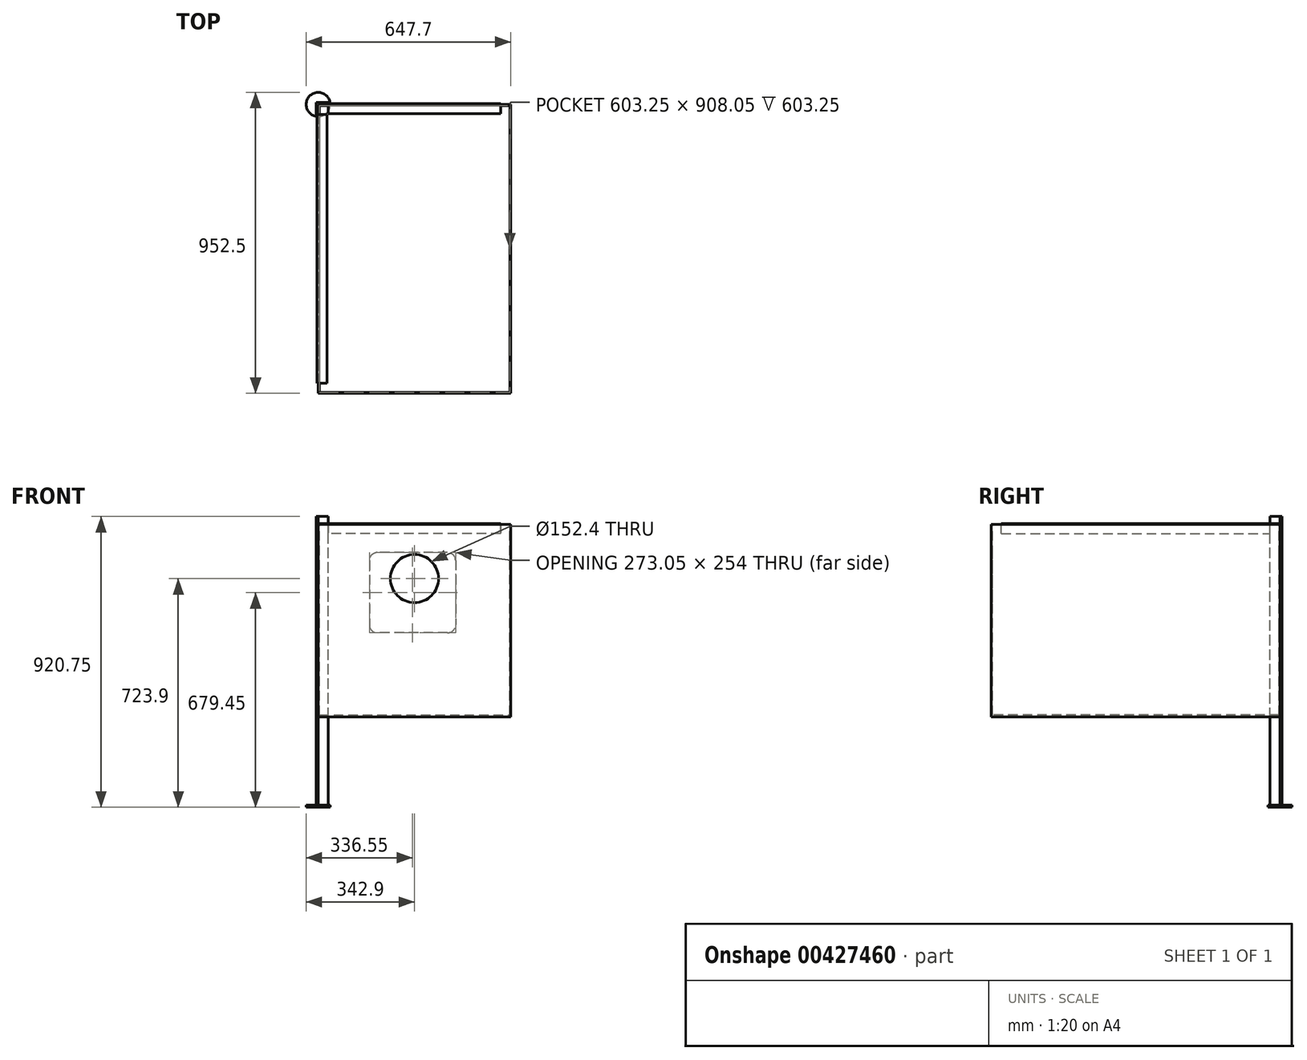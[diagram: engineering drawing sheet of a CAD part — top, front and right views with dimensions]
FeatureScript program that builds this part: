
annotation { "Feature Type Name" : "Feature", "Feature Type Description" : "" }
export const myFeature = defineFeature(function(context is Context, id is Id, definition is map)
    precondition{}
    {
        {
            var Q0;
            Q0=qCreatedBy(makeId("Top.planeOp"),FACE);
            var sketch = newSketch(context, id + "F0", { "sketchPlane" : qUnion([Q0])});
            skLineSegment(sketch, "E0.bottom", {"start": v(0, 0) * mm, "end": v(609.6, 0) * mm});
            skLineSegment(sketch, "E0.top", {"start": v(0, -914.4) * mm, "end": v(609.6, -914.4) * mm});
            skLineSegment(sketch, "E0.left", {"start": v(0, 0) * mm, "end": v(0, -914.4) * mm});
            skLineSegment(sketch, "E0.right", {"start": v(609.6, 0) * mm, "end": v(609.6, -914.4) * mm});
            skSolve(sketch);
        }
        {
            var Q0;
            Q0 = qSketchRegion(id + "F0", true);
            extrude(context, id + "F1", {"entities" : qUnion([Q0]), "depth" : 609.6 * mm});
        }
        {
            var Q0;
            Q0=makeQuery(id+"F1.opExtrude","CAP_FACE",FACE,{"disambiguationData":[OSD([sQuery(id+"F0.wireOp",EDGE,"E0.bottom"),sQuery(id+"F0.wireOp",EDGE,"E0.top"),sQuery(id+"F0.wireOp",EDGE,"E0.left"),sQuery(id+"F0.wireOp",EDGE,"E0.right")])],"isStart":false});
            var sketch = newSketch(context, id + "F2", { "sketchPlane" : qUnion([Q0])});
            skLineSegment(sketch, "E1.bottom", {"start": v(3.17, -3.17) * mm, "end": v(606.43, -3.17) * mm});
            skLineSegment(sketch, "E1.top", {"start": v(3.17, -911.23) * mm, "end": v(606.43, -911.23) * mm});
            skLineSegment(sketch, "E1.left", {"start": v(3.18, -3.18) * mm, "end": v(3.18, -911.23) * mm});
            skLineSegment(sketch, "E1.right", {"start": v(606.43, -3.17) * mm, "end": v(606.43, -911.22) * mm});
            skSolve(sketch);
        }
        {
            var Q0;
            Q0=makeQuery(id+"F2.imprint","IMPRINT",FACE,{"disambiguationData":[TD([[makeQuery(id+"F2.imprint","IMPRINT",EDGE,{"derivedFrom":sQuery(id+"F2.wireOp",EDGE,"E1.bottom")}),-1.0]])]});
            extrude(context, id + "F3", {"entities" : qUnion([Q0]), "operationType" : NewBodyOperationType.REMOVE, "oppositeDirection" : true, "depth" : 603.25 * mm});
        }
        {
            var Q0;
            Q0=makeQuery(id+"F1.opExtrude","SWEPT_FACE",FACE,{"disambiguationData":[OSD([sQuery(id+"F0.wireOp",EDGE,"E0.top")])]});
            var sketch = newSketch(context, id + "F4", { "sketchPlane" : qUnion([Q0])});
            skCircle(sketch, "E2", {"center": v(304.8, 438.15) * mm, "radius": 76.2 * mm});
            skSolve(sketch);
        }
        {
            var Q0;
            Q0=makeQuery(id+"F4.imprint","IMPRINT",FACE,{"disambiguationData":[TD([[makeQuery(id+"F4.imprint","IMPRINT",EDGE,{"derivedFrom":sQuery(id+"F4.wireOp",EDGE,"E2")}),1.0]])]});
            extrude(context, id + "F5", {"entities" : qUnion([Q0]), "operationType" : NewBodyOperationType.REMOVE, "oppositeDirection" : true, "depth" : 3.17 * mm});
        }
        {
            var Q0;
            Q0=makeQuery(id+"F1.opExtrude","CAP_FACE",FACE,{"disambiguationData":[OSD([sQuery(id+"F0.wireOp",EDGE,"E0.bottom"),sQuery(id+"F0.wireOp",EDGE,"E0.top"),sQuery(id+"F0.wireOp",EDGE,"E0.left"),sQuery(id+"F0.wireOp",EDGE,"E0.right")])],"isStart":false});
            var sketch = newSketch(context, id + "F6", { "sketchPlane" : qUnion([Q0])});
            skLineSegment(sketch, "E3", {"start": v(0, -31.75) * mm, "end": v(-6.35, -31.75) * mm});
            skLineSegment(sketch, "E4", {"start": v(-6.35, -31.75) * mm, "end": v(-6.35, 6.35) * mm});
            skLineSegment(sketch, "E5", {"start": v(-6.35, 6.35) * mm, "end": v(31.75, 6.35) * mm});
            skLineSegment(sketch, "E6", {"start": v(31.75, 6.35) * mm, "end": v(31.75, 0) * mm});
            skSolve(sketch);
        }
        {
            var Q0;
            {var subQ4=sQuery(id+"F6.wireOp",EDGE,"E3");Q0=makeQuery(id+"F6.imprint","IMPRINT",FACE,{"disambiguationData":[TD([[makeQuery(id+"F6.imprint","IMPRINT",EDGE,{"derivedFrom":subQ4}),-1.0]])]});}
            extrude(context, id + "F7", {"entities" : qUnion([Q0]), "oppositeDirection" : true, "depth" : 889 * mm});
        }
        {
            var Q0;
            Q0=makeQuery(id+"F7.opExtrude","CAP_FACE",FACE,{"disambiguationData":[OSD([sQuery(id+"F0.wireOp",EDGE,"E0.bottom"),sQuery(id+"F0.wireOp",EDGE,"E0.left"),sQuery(id+"F6.wireOp",EDGE,"E3"),sQuery(id+"F6.wireOp",EDGE,"E4"),sQuery(id+"F6.wireOp",EDGE,"E5"),sQuery(id+"F6.wireOp",EDGE,"E6")])],"isStart":true});
            extrude(context, id + "F8", {"entities" : qUnion([Q0]), "operationType" : NewBodyOperationType.ADD, "depth" : 25.4 * mm});
        }
        {
            var Q0;
            Q0=makeQuery(id+"F7.opExtrude","CAP_FACE",FACE,{"disambiguationData":[OSD([sQuery(id+"F0.wireOp",EDGE,"E0.bottom"),sQuery(id+"F0.wireOp",EDGE,"E0.left"),sQuery(id+"F6.wireOp",EDGE,"E3"),sQuery(id+"F6.wireOp",EDGE,"E4"),sQuery(id+"F6.wireOp",EDGE,"E5"),sQuery(id+"F6.wireOp",EDGE,"E6")])],"isStart":false});
            var sketch = newSketch(context, id + "F9", { "sketchPlane" : qUnion([Q0])});
            skCircle(sketch, "E7", {"center": v(0, 0) * mm, "radius": 38.1 * mm});
            skSolve(sketch);
        }
        {
            var Q0;
            Q0 = qSketchRegion(id + "F9", true);
            extrude(context, id + "F10", {"entities" : qUnion([Q0]), "operationType" : NewBodyOperationType.ADD, "depth" : 6.35 * mm});
        }
        {
            var Q0;
            Q0=makeQuery(id+"F1.opExtrude","SWEPT_FACE",FACE,{"disambiguationData":[OSD([sQuery(id+"F0.wireOp",EDGE,"E0.bottom")])]});
            var sketch = newSketch(context, id + "F11", { "sketchPlane" : qUnion([Q0])});
            skLineSegment(sketch, "E8.bottom", {"start": v(-409.58, 520.7) * mm, "end": v(-187.32, 520.7) * mm});
            skLineSegment(sketch, "E8.top", {"start": v(-409.58, 266.7) * mm, "end": v(-187.32, 266.7) * mm});
            skLineSegment(sketch, "E8.left", {"start": v(-434.98, 495.3) * mm, "end": v(-434.98, 292.1) * mm});
            skLineSegment(sketch, "E8.right", {"start": v(-161.92, 495.3) * mm, "end": v(-161.92, 292.1) * mm});
            skPoint(sketch, "E9.visualSharp", {"position": v(-434.98, 520.7) * mm});
            skArc(sketch, "E9.filletArc", {"start": v(-409.58, 520.7) * mm, "mid": v(-427.54, 513.26) * mm, "end": v(-434.98, 495.3) * mm});
            skPoint(sketch, "E10.visualSharp", {"position": v(-161.92, 520.7) * mm});
            skArc(sketch, "E10.filletArc", {"start": v(-161.92, 495.3) * mm, "mid": v(-169.36, 513.26) * mm, "end": v(-187.32, 520.7) * mm});
            skPoint(sketch, "E11.visualSharp", {"position": v(-161.92, 266.7) * mm});
            skArc(sketch, "E11.filletArc", {"start": v(-187.32, 266.7) * mm, "mid": v(-169.36, 274.14) * mm, "end": v(-161.92, 292.1) * mm});
            skPoint(sketch, "E12.visualSharp", {"position": v(-434.98, 266.7) * mm});
            skArc(sketch, "E12.filletArc", {"start": v(-434.98, 292.1) * mm, "mid": v(-427.54, 274.14) * mm, "end": v(-409.58, 266.7) * mm});
            skSolve(sketch);
        }
        {
            var Q0;
            Q0=makeQuery(id+"F11.imprint","IMPRINT",FACE,{"disambiguationData":[TD([[makeQuery(id+"F11.imprint","IMPRINT",EDGE,{"derivedFrom":sQuery(id+"F11.wireOp",EDGE,"E8.bottom")}),-1.0]])]});
            extrude(context, id + "F12", {"entities" : qUnion([Q0]), "operationType" : NewBodyOperationType.REMOVE, "oppositeDirection" : true, "depth" : 3.17 * mm});
        }
        {
            var Q0;
            {var subQ0=sQuery(id+"F6.wireOp",EDGE,"E6");Q0=makeQuery(id+"F8.boolean.opBoolean","MERGE",FACE,{"derivedFrom":[makeQuery(id+"F7.opExtrude","SWEPT_FACE",FACE,{"disambiguationData":[OSD([subQ0])]}),makeQuery(id+"F8.opExtrude","SWEPT_FACE",FACE,{"disambiguationData":[OSD([subQ0])]})]});}
            var sketch = newSketch(context, id + "F13", { "sketchPlane" : qUnion([Q0])});
            skLineSegment(sketch, "E13", {"start": v(0, 581.02) * mm, "end": v(0, 609.6) * mm});
            skLineSegment(sketch, "E14", {"start": v(0, 609.6) * mm, "end": v(-28.58, 609.6) * mm});
            skLineSegment(sketch, "E15", {"start": v(-28.58, 609.6) * mm, "end": v(-28.58, 612.77) * mm});
            skLineSegment(sketch, "E16", {"start": v(-28.58, 612.77) * mm, "end": v(3.17, 612.77) * mm});
            skLineSegment(sketch, "E17", {"start": v(3.17, 612.77) * mm, "end": v(3.17, 581.02) * mm});
            skLineSegment(sketch, "E18", {"start": v(3.17, 581.02) * mm, "end": v(0, 581.02) * mm});
            skSolve(sketch);
        }
        {
            var Q0;
            {var subQ6=sQuery(id+"F13.wireOp",EDGE,"E13");Q0=makeQuery(id+"F13.imprint","IMPRINT",FACE,{"disambiguationData":[TD([[makeQuery(id+"F13.imprint","IMPRINT",EDGE,{"derivedFrom":subQ6}),-1.0]])]});}
            var Q1;
            {var subQ0=sQuery(id+"F13.wireOp",EDGE,"E14");Q1=makeQuery(id+"F13.imprint","IMPRINT",FACE,{"disambiguationData":[TD([[makeQuery(id+"F13.imprint","IMPRINT",EDGE,{"derivedFrom":subQ0}),-1.0]])]});}
            extrude(context, id + "F14", {"entities" : qUnion([Q0, Q1]), "depth" : 546.1 * mm});
        }
        {
            var Q0;
            {var subQ0=sQuery(id+"F6.wireOp",EDGE,"E3");Q0=makeQuery(id+"F8.boolean.opBoolean","MERGE",FACE,{"derivedFrom":[makeQuery(id+"F7.opExtrude","SWEPT_FACE",FACE,{"disambiguationData":[OSD([subQ0])]}),makeQuery(id+"F8.opExtrude","SWEPT_FACE",FACE,{"disambiguationData":[OSD([subQ0])]})]});}
            var sketch = newSketch(context, id + "F15", { "sketchPlane" : qUnion([Q0])});
            skLineSegment(sketch, "E19", {"start": v(28.57, 609.6) * mm, "end": v(0, 609.6) * mm});
            skLineSegment(sketch, "E20", {"start": v(0, 609.6) * mm, "end": v(0, 581.02) * mm});
            skLineSegment(sketch, "E21", {"start": v(0, 581.02) * mm, "end": v(-3.18, 581.02) * mm});
            skLineSegment(sketch, "E22", {"start": v(-3.18, 581.02) * mm, "end": v(-3.18, 612.77) * mm});
            skLineSegment(sketch, "E23", {"start": v(-3.18, 612.77) * mm, "end": v(28.57, 612.77) * mm});
            skLineSegment(sketch, "E24", {"start": v(28.58, 612.77) * mm, "end": v(28.58, 609.6) * mm});
            skSolve(sketch);
        }
        {
            var Q0;
            {var subQ6=sQuery(id+"F15.wireOp",EDGE,"E20");Q0=makeQuery(id+"F15.imprint","IMPRINT",FACE,{"disambiguationData":[TD([[makeQuery(id+"F15.imprint","IMPRINT",EDGE,{"derivedFrom":subQ6}),1.0]])]});}
            var Q1;
            {var subQ0=sQuery(id+"F15.wireOp",EDGE,"E19");Q1=makeQuery(id+"F15.imprint","IMPRINT",FACE,{"disambiguationData":[TD([[makeQuery(id+"F15.imprint","IMPRINT",EDGE,{"derivedFrom":subQ0}),-1.0]])]});}
            extrude(context, id + "F16", {"entities" : qUnion([Q0, Q1]), "depth" : 850.9 * mm});
        }
    });
